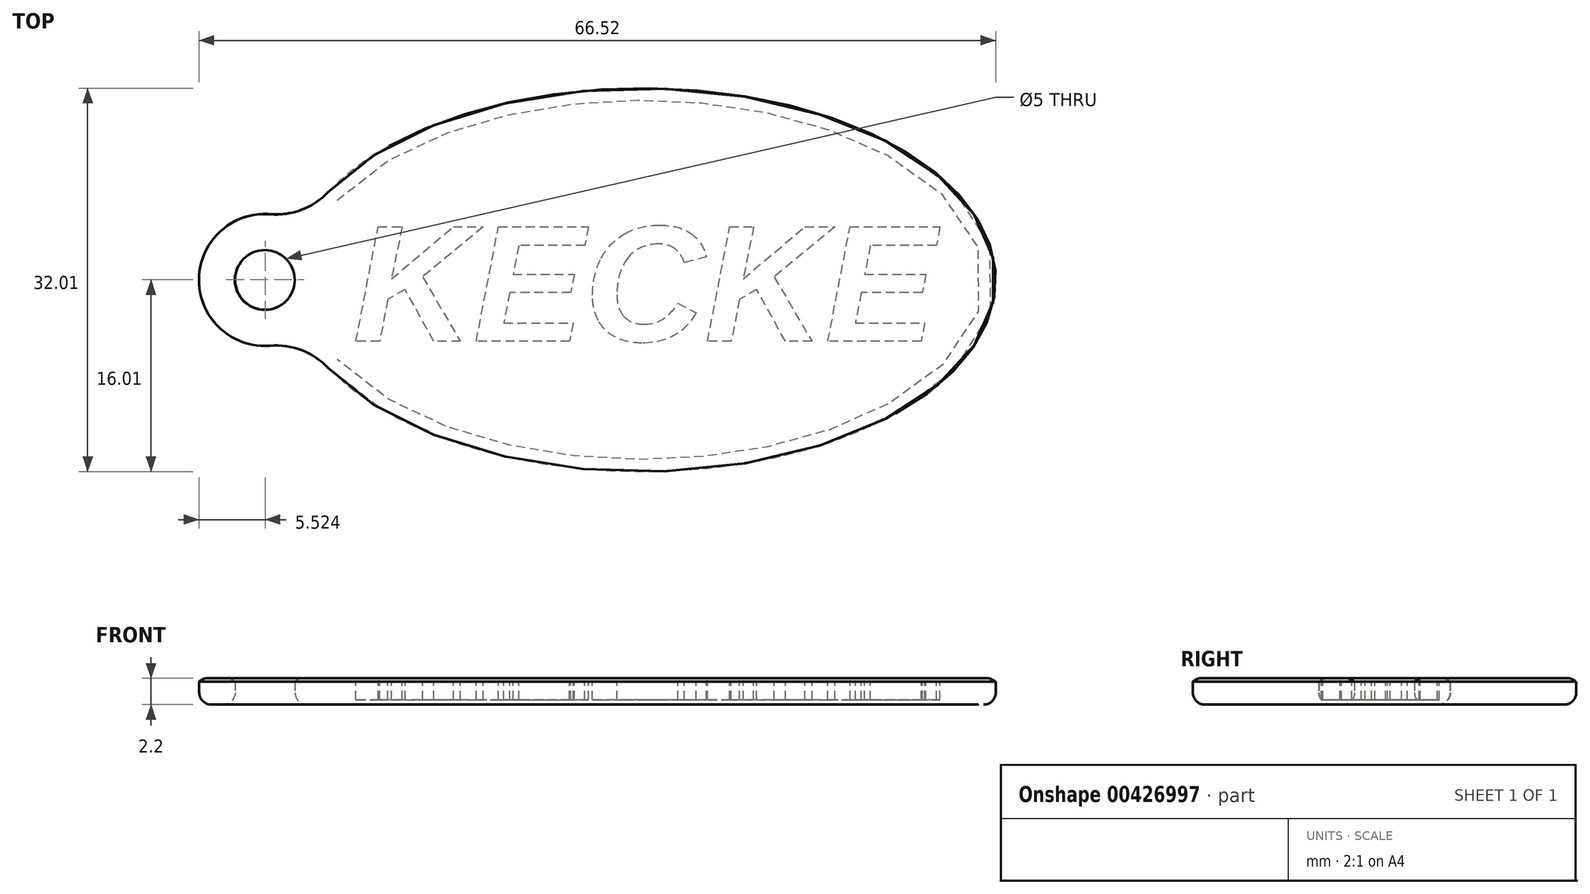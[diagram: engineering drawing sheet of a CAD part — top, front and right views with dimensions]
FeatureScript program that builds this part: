
annotation { "Feature Type Name" : "Feature", "Feature Type Description" : "" }
export const myFeature = defineFeature(function(context is Context, id is Id, definition is map)
    precondition{}
    {
        {
            var Q0;
            Q0=qCreatedBy(makeId("Top.planeOp"),FACE);
            var sketch = newSketch(context, id + "F0", { "sketchPlane" : qUnion([Q0])});
            skEllipticalArc(sketch, "E0", {});
            skArc(sketch, "E1", {"start": v(-5.86, 5.48) * mm, "mid": v(-11.8, 0) * mm, "end": v(-5.86, -5.48) * mm});
            skCircle(sketch, "E2", {"center": v(-6.3, 0) * mm, "radius": 2.5 * mm});
            skPoint(sketch, "E3.visualSharp", {"position": v(-3.12, 4.49) * mm});
            skArc(sketch, "E3.filletArc", {"start": v(-5.86, 5.48) * mm, "mid": v(-3.24, 5.86) * mm, "end": v(-1.03, 7.33) * mm});
            skPoint(sketch, "E4.visualSharp", {"position": v(-3.12, -4.49) * mm});
            skArc(sketch, "E4.filletArc", {"start": v(-1.03, -7.33) * mm, "mid": v(-3.24, -5.86) * mm, "end": v(-5.86, -5.48) * mm});
            const initialGuessF0  = {"E0": [0.02519380171723914, 1.357887608159041e-10, 1, 0, 0.0295, 0.016, 3.6174484728170166, 2.665736834362569]};
            skSetInitialGuess(sketch, initialGuessF0);
            skSolve(sketch);
        }
        {
            var Q0;
            Q0=makeQuery(id+"F0.imprint","IMPRINT",FACE,{"disambiguationData":[TD([[makeQuery(id+"F0.imprint","IMPRINT",EDGE,{"derivedFrom":sQuery(id+"F0.wireOp",EDGE,"E0")}),1.0]])]});
            extrude(context, id + "F1", {"entities" : qUnion([Q0]), "depth" : 1.9 * mm});
        }
        {
            var Q0;
            Q0=makeQuery(id+"F1.opExtrude","CAP_FACE",FACE,{"disambiguationData":[OSD([sQuery(id+"F0.wireOp",EDGE,"E0"),sQuery(id+"F0.wireOp",EDGE,"E1"),sQuery(id+"F0.wireOp",EDGE,"E2"),sQuery(id+"F0.wireOp",EDGE,"E3.filletArc"),sQuery(id+"F0.wireOp",EDGE,"E4.filletArc")])],"isStart":false});
            var sketch = newSketch(context, id + "F2", { "sketchPlane" : qUnion([Q0])});
            skText(sketch, "E5", { "text": "KECKE", "fontName": "Arimo-BoldItalic.ttf"});
            const initialGuessF2  = {"E5": [0.00103, -0.00514, 1, 0, 0.01001]};
            skSetInitialGuess(sketch, initialGuessF2);
            skSolve(sketch);
        }
        {
            var Q0;
            Q0=makeQuery(id+"F1.opExtrude","CAP_EDGE",EDGE,{"disambiguationData":[OSD([sQuery(id+"F0.wireOp",EDGE,"E0")])],"isStart":true});
            var Q1;
            Q1=makeQuery(id+"F1.opExtrude","CAP_EDGE",EDGE,{"disambiguationData":[OSD([sQuery(id+"F0.wireOp",EDGE,"E4.filletArc")])],"isStart":true});
            var Q2;
            Q2=makeQuery(id+"F1.opExtrude","CAP_EDGE",EDGE,{"disambiguationData":[OSD([sQuery(id+"F0.wireOp",EDGE,"E1")])],"isStart":true});
            var Q3;
            Q3=makeQuery(id+"F1.opExtrude","CAP_EDGE",EDGE,{"disambiguationData":[OSD([sQuery(id+"F0.wireOp",EDGE,"E3.filletArc")])],"isStart":true});
            fillet(context, id + "F3", {"entities" : qUnion([Q0, Q1, Q2, Q3]), "radius" : 1 * mm, "tangentPropagation" : true, "allowEdgeOverflow" : false});
        }
        {
            var Q0;
            Q0=makeQuery(id+"FOT0X1xBIzvd5YW_1.opExtrude","CAP_EDGE",EDGE,{"disambiguationData":[OSD([sQuery(id+"F0.wireOp",EDGE,"E2")])],"isStart":false});
            var Q1;
            Q1=makeQuery(id+"F1.opExtrude","CAP_EDGE",EDGE,{"disambiguationData":[OSD([sQuery(id+"F0.wireOp",EDGE,"E2")])],"isStart":true});
            fillet(context, id + "F4", {"entities" : qUnion([Q0, Q1]), "radius" : 1 * mm, "tangentPropagation" : true, "allowEdgeOverflow" : false});
        }
        {
            var Q0;
            Q0=makeQuery(id+"F2.imprint","IMPRINT",FACE,{"disambiguationData":[TD([[makeQuery(id+"F2.imprint","IMPRINT",EDGE,{"derivedFrom":sQuery(id+"F2.wireOp",EDGE,"E5.sketch_text.stroke-0")}),-1.0]])]});
            var Q1;
            Q1=makeQuery(id+"F2.imprint","IMPRINT",FACE,{"disambiguationData":[TD([[makeQuery(id+"F2.imprint","IMPRINT",EDGE,{"derivedFrom":sQuery(id+"F2.wireOp",EDGE,"E5.sketch_text.stroke-29")}),-1.0]])]});
            var Q2;
            Q2=makeQuery(id+"F2.imprint","IMPRINT",FACE,{"disambiguationData":[TD([[makeQuery(id+"F2.imprint","IMPRINT",EDGE,{"derivedFrom":sQuery(id+"F2.wireOp",EDGE,"E5.sketch_text.stroke-33")}),-1.0]])]});
            var Q3;
            Q3=makeQuery(id+"F2.imprint","IMPRINT",FACE,{"disambiguationData":[TD([[makeQuery(id+"F2.imprint","IMPRINT",EDGE,{"derivedFrom":sQuery(id+"F2.wireOp",EDGE,"E5.sketch_text.stroke-46")}),-1.0]])]});
            var Q4;
            Q4=makeQuery(id+"F2.imprint","IMPRINT",FACE,{"disambiguationData":[TD([[makeQuery(id+"F2.imprint","IMPRINT",EDGE,{"derivedFrom":sQuery(id+"F2.wireOp",EDGE,"E5.sketch_text.stroke-50")}),-1.0]])]});
            var Q5;
            Q5=makeQuery(id+"F2.imprint","IMPRINT",FACE,{"disambiguationData":[TD([[makeQuery(id+"F2.imprint","IMPRINT",EDGE,{"derivedFrom":sQuery(id+"F2.wireOp",EDGE,"E5.sketch_text.stroke-62")}),-1.0]])]});
            var Q6;
            Q6=makeQuery(id+"F2.imprint","IMPRINT",FACE,{"disambiguationData":[TD([[makeQuery(id+"F2.imprint","IMPRINT",EDGE,{"derivedFrom":sQuery(id+"F2.wireOp",EDGE,"E5.sketch_text.stroke-74")}),-1.0]])]});
            var Q7;
            Q7=makeQuery(id+"F2.imprint","IMPRINT",FACE,{"disambiguationData":[TD([[makeQuery(id+"F2.imprint","IMPRINT",EDGE,{"derivedFrom":sQuery(id+"F2.wireOp",EDGE,"E5.sketch_text.stroke-12")}),-1.0]])]});
            extrude(context, id + "F5", {"entities" : qUnion([Q0, Q1, Q2, Q3, Q4, Q5, Q6, Q7]), "operationType" : NewBodyOperationType.REMOVE, "oppositeDirection" : true, "depth" : 1.5 * mm});
        }
        {
            var Q0;
            Q0=makeQuery(id+"F2.imprint","IMPRINT",FACE,{"disambiguationData":[TD([[makeQuery(id+"F2.imprint","IMPRINT",EDGE,{"derivedFrom":sQuery(id+"F2.wireOp",EDGE,"E5.sketch_text.stroke-0")}),1.0]])]});
            var sketch = newSketch(context, id + "F6", { "sketchPlane" : qUnion([Q0])});
            skEllipticalArc(sketch, "E6", {});
            skArc(sketch, "E7", {"start": v(-5.89, 5.47) * mm, "mid": v(-11.83, -0.01) * mm, "end": v(-5.89, -5.5) * mm});
            skCircle(sketch, "E8", {"center": v(-6.33, -0.01) * mm, "radius": 2.5 * mm});
            skPoint(sketch, "E9.visualSharp", {"position": v(-3.15, 4.47) * mm});
            skArc(sketch, "E9.filletArc", {"start": v(-5.89, 5.47) * mm, "mid": v(-3.26, 5.84) * mm, "end": v(-1.06, 7.31) * mm});
            skPoint(sketch, "E10.visualSharp", {"position": v(-3.15, -4.5) * mm});
            skArc(sketch, "E10.filletArc", {"start": v(-1.06, -7.34) * mm, "mid": v(-3.26, -5.87) * mm, "end": v(-5.89, -5.5) * mm});
            const initialGuessF6  = {"E6": [0.025167490923183683, -1.4673782696881035e-05, 1, 0, 0.0295, 0.016, 3.617448472817016, 2.665736834362569]};
            skSetInitialGuess(sketch, initialGuessF6);
            skSolve(sketch);
        }
        {
            var Q0;
            Q0 = qSketchRegion(id + "F6", true);
            extrude(context, id + "F7", {"entities" : qUnion([Q0]), "depth" : 0.3 * mm});
        }
        {
            var Q0;
            Q0=makeQuery(id+"F7.opExtrude","CAP_EDGE",EDGE,{"disambiguationData":[OSD([sQuery(id+"F6.wireOp",EDGE,"E6")])],"isStart":false});
            var Q1;
            Q1=makeQuery(id+"F7.opExtrude","CAP_EDGE",EDGE,{"disambiguationData":[OSD([sQuery(id+"F6.wireOp",EDGE,"E10.filletArc")])],"isStart":false});
            var Q2;
            Q2=makeQuery(id+"F7.opExtrude","CAP_EDGE",EDGE,{"disambiguationData":[OSD([sQuery(id+"F6.wireOp",EDGE,"E7")])],"isStart":false});
            var Q3;
            Q3=makeQuery(id+"F7.opExtrude","CAP_EDGE",EDGE,{"disambiguationData":[OSD([sQuery(id+"F6.wireOp",EDGE,"E9.filletArc")])],"isStart":false});
            var Q4;
            Q4=makeQuery(id+"F7.opExtrude","CAP_EDGE",EDGE,{"disambiguationData":[OSD([sQuery(id+"F6.wireOp",EDGE,"E8")])],"isStart":false});
            fillet(context, id + "F8", {"entities" : qUnion([Q0, Q1, Q2, Q3, Q4]), "radius" : 1 * mm, "tangentPropagation" : true, "allowEdgeOverflow" : false});
        }
    });
